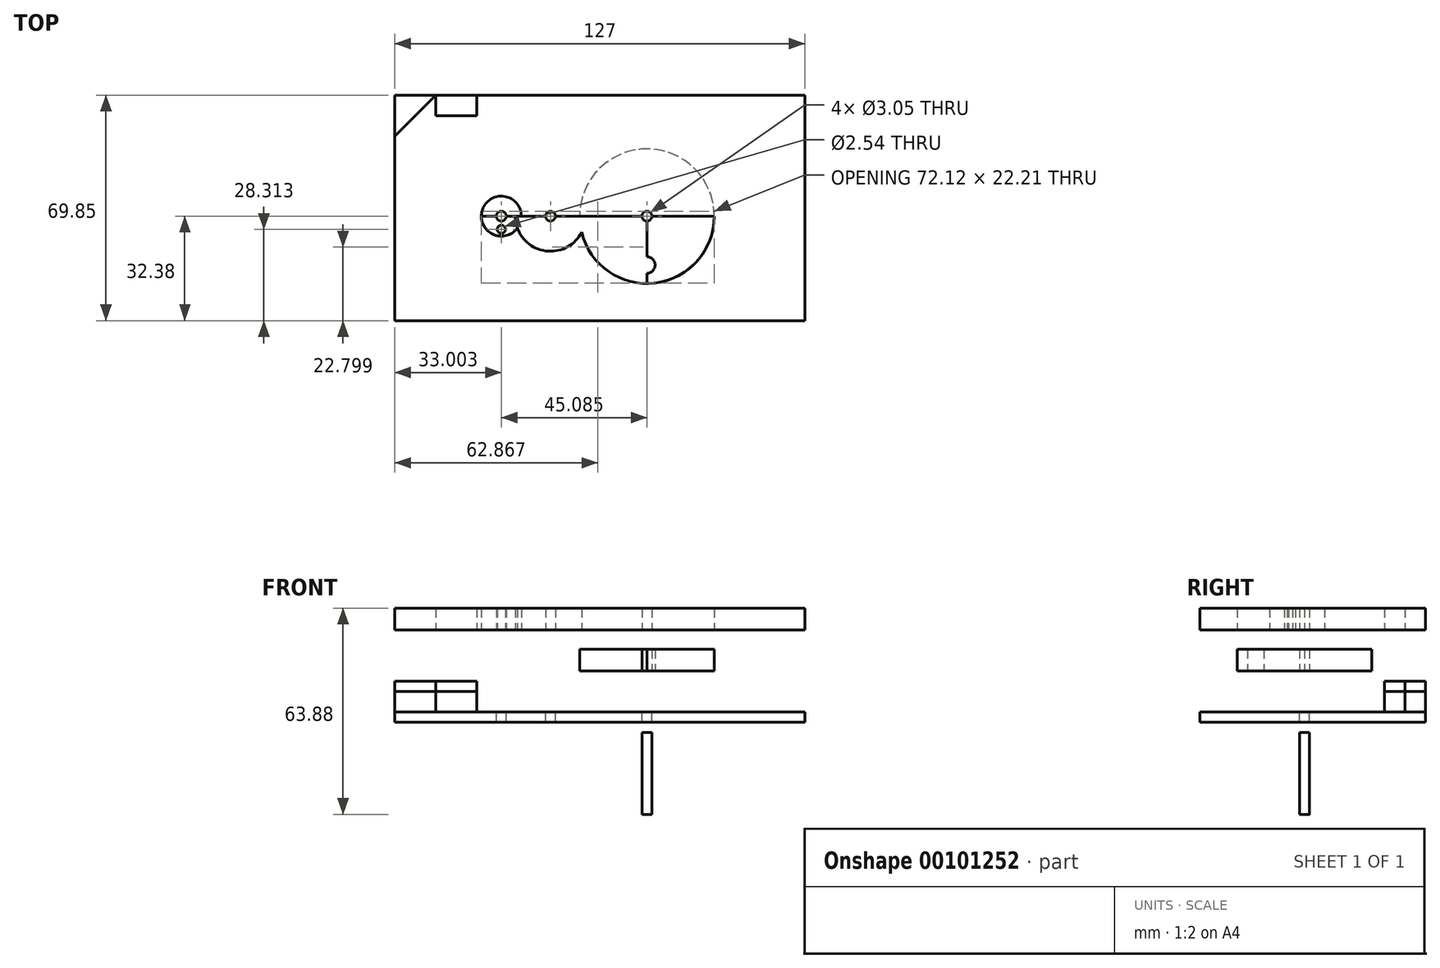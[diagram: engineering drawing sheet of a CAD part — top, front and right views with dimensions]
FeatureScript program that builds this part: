
annotation { "Feature Type Name" : "Feature", "Feature Type Description" : "" }
export const myFeature = defineFeature(function(context is Context, id is Id, definition is map)
    precondition{}
    {
        {
            var Q0;
            Q0=qCreatedBy(makeId("Top.planeOp"),FACE);
            var sketch = newSketch(context, id + "F0", { "sketchPlane" : qUnion([Q0])});
            skLineSegment(sketch, "E0", {"start": v(-33.34, 3.44) * mm, "end": v(-18.12, 3.44) * mm});
            skLineSegment(sketch, "E1", {"start": v(-18.12, 3.44) * mm, "end": v(11.75, 3.44) * mm});
            skCircle(sketch, "E2", {"center": v(-33.34, 3.44) * mm, "radius": 6.2 * mm});
            skCircle(sketch, "E3", {"center": v(11.75, 3.44) * mm, "radius": 20.84 * mm});
            skCircle(sketch, "E4", {"center": v(-18.12, 3.44) * mm, "radius": 10.86 * mm});
            skLineSegment(sketch, "E5.bottom", {"start": v(-66.34, 40.9) * mm, "end": v(60.66, 40.9) * mm});
            skLineSegment(sketch, "E5.top", {"start": v(-66.34, -28.94) * mm, "end": v(60.66, -28.94) * mm});
            skLineSegment(sketch, "E5.left", {"start": v(-66.34, 40.9) * mm, "end": v(-66.34, -28.94) * mm});
            skLineSegment(sketch, "E5.right", {"start": v(60.66, 40.9) * mm, "end": v(60.66, -28.94) * mm});
            skCircle(sketch, "E6", {"center": v(11.75, 3.44) * mm, "radius": 1.52 * mm});
            skCircle(sketch, "E7", {"center": v(-18.12, 3.44) * mm, "radius": 1.52 * mm});
            skCircle(sketch, "E8", {"center": v(-33.34, 3.44) * mm, "radius": 1.52 * mm});
            skLineSegment(sketch, "E9", {"start": v(11.75, 3.44) * mm, "end": v(11.75, -17.4) * mm});
            skLineSegment(sketch, "E10", {"start": v(-18.12, 3.44) * mm, "end": v(-18.27, -7.42) * mm});
            skLineSegment(sketch, "E11", {"start": v(-33.34, 3.44) * mm, "end": v(-33.34, -2.76) * mm});
            skCircle(sketch, "E12", {"center": v(11.75, -11.68) * mm, "radius": 2.54 * mm});
            skCircle(sketch, "E13", {"center": v(-18.23, -4.37) * mm, "radius": 1.9 * mm});
            skCircle(sketch, "E14", {"center": v(-33.34, -0.63) * mm, "radius": 1.27 * mm});
            skLineSegment(sketch, "E15", {"start": v(-53.64, 40.9) * mm, "end": v(-66.34, 28.2) * mm});
            skLineSegment(sketch, "E16", {"start": v(-53.64, 40.9) * mm, "end": v(-53.64, 34.56) * mm});
            skLineSegment(sketch, "E17", {"start": v(-53.64, 34.56) * mm, "end": v(-40.94, 34.56) * mm});
            skLineSegment(sketch, "E18", {"start": v(-40.94, 34.56) * mm, "end": v(-40.94, 40.9) * mm});
            skLineSegment(sketch, "E19", {"start": v(-39.54, 3.44) * mm, "end": v(32.59, 3.44) * mm});
            skLineSegment(sketch, "E20", {"start": v(-3.47, 3.44) * mm, "end": v(-3.47, 9.38) * mm});
            skSolve(sketch);
        }
        {
            var Q0;
            Q0=makeQuery(id+"F0.imprint","IMPRINT",FACE,{"disambiguationData":[TD([[makeQuery(id+"F0.imprint","IMPRINT",EDGE,{"derivedFrom":sQuery(id+"F0.wireOp",EDGE,"E5.bottom")}),-1.0]])]});
            var Q1;
            Q1=makeQuery(id+"F0.imprint","IMPRINT",FACE,{"disambiguationData":[TD([[makeQuery(id+"F0.imprint","IMPRINT",EDGE,{"derivedFrom":sQuery(id+"F0.wireOp",EDGE,"E6")}),-1.0]])]});
            var Q2;
            {var subQ6=sQuery(id+"F0.wireOp",EDGE,"E0");var subQ9=sQuery(id+"F0.wireOp",EDGE,"E2");var subQ10=makeQuery(id+"F0.imprint","INTERSECT",VERTEX,{"derivedFrom":[subQ6,subQ9]});Q2=makeQuery(id+"F0.imprint","IMPRINT",FACE,{"disambiguationData":[TD([[makeQuery(id+"F0.imprint","IMPRINT",EDGE,{"disambiguationData":[TD([[subQ10,-1.0]])],"derivedFrom":subQ6}),1.0]])]});}
            var Q3;
            Q3=makeQuery(id+"F0.imprint","IMPRINT",FACE,{"disambiguationData":[TD([[makeQuery(id+"F0.imprint","IMPRINT",EDGE,{"derivedFrom":sQuery(id+"F0.wireOp",EDGE,"E8")}),-1.0]])]});
            var Q4;
            {var subQ0=sQuery(id+"F0.wireOp",EDGE,"E4");var subQ1=sQuery(id+"F0.wireOp",EDGE,"E0");var subQ2=makeQuery(id+"F0.imprint","INTERSECT",VERTEX,{"derivedFrom":[subQ1,subQ0]});Q4=makeQuery(id+"F0.imprint","IMPRINT",FACE,{"disambiguationData":[TD([[makeQuery(id+"F0.imprint","IMPRINT",EDGE,{"disambiguationData":[TD([[subQ2,-1.0]])],"derivedFrom":subQ1}),-1.0]])]});}
            var Q5;
            {var subQ0=sQuery(id+"F0.wireOp",EDGE,"E4");var subQ1=sQuery(id+"F0.wireOp",EDGE,"E0");var subQ2=makeQuery(id+"F0.imprint","INTERSECT",VERTEX,{"derivedFrom":[subQ1,subQ0]});Q5=makeQuery(id+"F0.imprint","IMPRINT",FACE,{"disambiguationData":[TD([[makeQuery(id+"F0.imprint","IMPRINT",EDGE,{"disambiguationData":[TD([[subQ2,-1.0]])],"derivedFrom":subQ1}),1.0]])]});}
            var Q6;
            {var subQ0=sQuery(id+"F0.wireOp",EDGE,"E4");var subQ1=sQuery(id+"F0.wireOp",EDGE,"E1");var subQ2=makeQuery(id+"F0.imprint","INTERSECT",VERTEX,{"derivedFrom":[subQ1,subQ0]});Q6=makeQuery(id+"F0.imprint","IMPRINT",FACE,{"disambiguationData":[TD([[makeQuery(id+"F0.imprint","IMPRINT",EDGE,{"disambiguationData":[TD([[subQ2,1.0]])],"derivedFrom":subQ1}),-1.0]])]});}
            var Q7;
            {var subQ0=sQuery(id+"F0.wireOp",EDGE,"E4");var subQ1=sQuery(id+"F0.wireOp",EDGE,"E1");var subQ2=makeQuery(id+"F0.imprint","INTERSECT",VERTEX,{"derivedFrom":[subQ1,subQ0]});Q7=makeQuery(id+"F0.imprint","IMPRINT",FACE,{"disambiguationData":[TD([[makeQuery(id+"F0.imprint","IMPRINT",EDGE,{"disambiguationData":[TD([[subQ2,1.0]])],"derivedFrom":subQ1}),1.0]])]});}
            var Q8;
            {var subQ0=sQuery(id+"F0.wireOp",EDGE,"kLhhA65f-NG9x-GNjo-BDkE-ldiiMeL40Zhi");var subQ1=sQuery(id+"F0.wireOp",EDGE,"E11");var subQ2=makeQuery(id+"F0.imprint","INTERSECT",VERTEX,{"derivedFrom":[subQ1,subQ0]});Q8=makeQuery(id+"F0.imprint","IMPRINT",FACE,{"disambiguationData":[TD([[makeQuery(id+"F0.imprint","IMPRINT",EDGE,{"disambiguationData":[TD([[subQ2,-1.0]])],"derivedFrom":subQ1}),-1.0]])]});}
            var Q9;
            {var subQ0=sQuery(id+"F0.wireOp",EDGE,"8ZkhhjgY-9uin-yOEb-Jnnh-ZfXHKx15u7Ma");var subQ1=sQuery(id+"F0.wireOp",EDGE,"E11");var subQ2=makeQuery(id+"F0.imprint","INTERSECT",VERTEX,{"derivedFrom":[subQ1,subQ0]});Q9=makeQuery(id+"F0.imprint","IMPRINT",FACE,{"disambiguationData":[TD([[makeQuery(id+"F0.imprint","IMPRINT",EDGE,{"disambiguationData":[TD([[subQ2,-1.0]])],"derivedFrom":subQ1}),-1.0]])]});}
            var Q10;
            {var subQ0=sQuery(id+"F0.wireOp",EDGE,"kLhhA65f-NG9x-GNjo-BDkE-ldiiMeL40Zhi");var subQ1=sQuery(id+"F0.wireOp",EDGE,"E11");var subQ2=makeQuery(id+"F0.imprint","INTERSECT",VERTEX,{"derivedFrom":[subQ1,subQ0]});Q10=makeQuery(id+"F0.imprint","IMPRINT",FACE,{"disambiguationData":[TD([[makeQuery(id+"F0.imprint","IMPRINT",EDGE,{"disambiguationData":[TD([[subQ2,-1.0]])],"derivedFrom":subQ1}),1.0]])]});}
            var Q11;
            {var subQ5=sQuery(id+"F0.wireOp",EDGE,"8ZkhhjgY-9uin-yOEb-Jnnh-ZfXHKx15u7Ma");var subQ7=sQuery(id+"F0.wireOp",EDGE,"E11");var subQ9=makeQuery(id+"F0.imprint","INTERSECT",VERTEX,{"derivedFrom":[subQ7,subQ5]});Q11=makeQuery(id+"F0.imprint","IMPRINT",FACE,{"disambiguationData":[TD([[makeQuery(id+"F0.imprint","IMPRINT",EDGE,{"disambiguationData":[TD([[subQ9,-1.0]])],"derivedFrom":subQ7}),1.0]])]});}
            var Q12;
            {var subQ0=sQuery(id+"F0.wireOp",EDGE,"8ZkhhjgY-9uin-yOEb-Jnnh-ZfXHKx15u7Ma");var subQ1=sQuery(id+"F0.wireOp",EDGE,"klJGlrE8-QjUh-doVU-lAX6-h4YymrU0E4Rz");var subQ2=makeQuery(id+"F0.imprint","INTERSECT",VERTEX,{"derivedFrom":[subQ1,subQ0]});Q12=makeQuery(id+"F0.imprint","IMPRINT",FACE,{"disambiguationData":[TD([[makeQuery(id+"F0.imprint","IMPRINT",EDGE,{"disambiguationData":[TD([[subQ2,-1.0]])],"derivedFrom":subQ1}),1.0]])]});}
            var Q13;
            {var subQ0=sQuery(id+"F0.wireOp",EDGE,"Twp39fOy-9zCw-zEIi-sOgK-c6f8t6DE6qxe");var subQ1=sQuery(id+"F0.wireOp",EDGE,"klJGlrE8-QjUh-doVU-lAX6-h4YymrU0E4Rz");var subQ2=makeQuery(id+"F0.imprint","INTERSECT",VERTEX,{"derivedFrom":[subQ1,subQ0]});Q13=makeQuery(id+"F0.imprint","IMPRINT",FACE,{"disambiguationData":[TD([[makeQuery(id+"F0.imprint","IMPRINT",EDGE,{"disambiguationData":[TD([[subQ2,1.0]])],"derivedFrom":subQ1}),-1.0]])]});}
            var Q14;
            {var subQ15=sQuery(id+"F0.wireOp",EDGE,"E8");var subQ20=sQuery(id+"F0.wireOp",EDGE,"E0");var subQ21=makeQuery(id+"F0.imprint","INTERSECT",VERTEX,{"derivedFrom":[subQ20,subQ15]});Q14=makeQuery(id+"F0.imprint","IMPRINT",FACE,{"disambiguationData":[TD([[makeQuery(id+"F0.imprint","IMPRINT",EDGE,{"disambiguationData":[TD([[subQ21,-1.0]])],"derivedFrom":subQ20}),-1.0]])]});}
            var Q15;
            {var subQ1=sQuery(id+"F0.wireOp",EDGE,"E7");var subQ15=sQuery(id+"F0.wireOp",EDGE,"E1");var subQ20=makeQuery(id+"F0.imprint","INTERSECT",VERTEX,{"derivedFrom":[subQ15,subQ1]});Q15=makeQuery(id+"F0.imprint","IMPRINT",FACE,{"disambiguationData":[TD([[makeQuery(id+"F0.imprint","IMPRINT",EDGE,{"disambiguationData":[TD([[subQ20,-1.0]])],"derivedFrom":subQ15}),-1.0]])]});}
            var Q16;
            {var subQ0=sQuery(id+"F0.wireOp",EDGE,"5052977a-4594-4a14-8260-0f098557343a");var subQ1=sQuery(id+"F0.wireOp",EDGE,"0b054047-080a-4dd0-b0d3-495809a409b5");var subQ2=makeQuery(id+"F0.imprint","INTERSECT",VERTEX,{"derivedFrom":[subQ1,subQ0]});Q16=makeQuery(id+"F0.imprint","IMPRINT",FACE,{"disambiguationData":[TD([[makeQuery(id+"F0.imprint","IMPRINT",EDGE,{"disambiguationData":[TD([[subQ2,-1.0]])],"derivedFrom":subQ1}),1.0]])]});}
            var Q17;
            {var subQ0=sQuery(id+"F0.wireOp",EDGE,"5fe9bd24-ed45-42ec-b14b-03178a733d0b");var subQ1=sQuery(id+"F0.wireOp",EDGE,"5052977a-4594-4a14-8260-0f098557343a");var subQ2=makeQuery(id+"F0.imprint","INTERSECT",VERTEX,{"derivedFrom":[subQ1,subQ0]});Q17=makeQuery(id+"F0.imprint","IMPRINT",FACE,{"disambiguationData":[TD([[makeQuery(id+"F0.imprint","IMPRINT",EDGE,{"disambiguationData":[TD([[subQ2,1.0]])],"derivedFrom":subQ1}),-1.0]])]});}
            var Q18;
            {var subQ0=sQuery(id+"F0.wireOp",EDGE,"AysafuJL-hgFW-WlnW-CkoB-AsvmlXaG8yLZ");var subQ1=sQuery(id+"F0.wireOp",EDGE,"0b054047-080a-4dd0-b0d3-495809a409b5");var subQ2=makeQuery(id+"F0.imprint","INTERSECT",VERTEX,{"derivedFrom":[subQ1,subQ0]});Q18=makeQuery(id+"F0.imprint","IMPRINT",FACE,{"disambiguationData":[TD([[makeQuery(id+"F0.imprint","IMPRINT",EDGE,{"disambiguationData":[TD([[subQ2,-1.0]])],"derivedFrom":subQ1}),-1.0]])]});}
            var Q19;
            {var subQ0=sQuery(id+"F0.wireOp",EDGE,"AysafuJL-hgFW-WlnW-CkoB-AsvmlXaG8yLZ");var subQ1=sQuery(id+"F0.wireOp",EDGE,"0b054047-080a-4dd0-b0d3-495809a409b5");var subQ2=makeQuery(id+"F0.imprint","INTERSECT",VERTEX,{"derivedFrom":[subQ1,subQ0]});Q19=makeQuery(id+"F0.imprint","IMPRINT",FACE,{"disambiguationData":[TD([[makeQuery(id+"F0.imprint","IMPRINT",EDGE,{"disambiguationData":[TD([[subQ2,-1.0]])],"derivedFrom":subQ1}),1.0]])]});}
            var Q20;
            {var subQ0=sQuery(id+"F0.wireOp",EDGE,"AysafuJL-hgFW-WlnW-CkoB-AsvmlXaG8yLZ");var subQ1=sQuery(id+"F0.wireOp",EDGE,"5fe9bd24-ed45-42ec-b14b-03178a733d0b");var subQ2=makeQuery(id+"F0.imprint","INTERSECT",VERTEX,{"derivedFrom":[subQ1,subQ0]});Q20=makeQuery(id+"F0.imprint","IMPRINT",FACE,{"disambiguationData":[TD([[makeQuery(id+"F0.imprint","IMPRINT",EDGE,{"disambiguationData":[TD([[subQ2,-1.0]])],"derivedFrom":subQ1}),-1.0]])]});}
            var Q21;
            {var subQ0=sQuery(id+"F0.wireOp",EDGE,"AysafuJL-hgFW-WlnW-CkoB-AsvmlXaG8yLZ");var subQ1=sQuery(id+"F0.wireOp",EDGE,"5fe9bd24-ed45-42ec-b14b-03178a733d0b");var subQ2=makeQuery(id+"F0.imprint","INTERSECT",VERTEX,{"derivedFrom":[subQ1,subQ0]});Q21=makeQuery(id+"F0.imprint","IMPRINT",FACE,{"disambiguationData":[TD([[makeQuery(id+"F0.imprint","IMPRINT",EDGE,{"disambiguationData":[TD([[subQ2,-1.0]])],"derivedFrom":subQ1}),1.0]])]});}
            var Q22;
            {var subQ0=sQuery(id+"F0.wireOp",EDGE,"fyqTDLPH-M1B6-Q20Z-5p9l-KNEeE5BD3CPC");var subQ1=sQuery(id+"F0.wireOp",EDGE,"5fe9bd24-ed45-42ec-b14b-03178a733d0b");var subQ2=makeQuery(id+"F0.imprint","INTERSECT",VERTEX,{"derivedFrom":[subQ1,subQ0]});Q22=makeQuery(id+"F0.imprint","IMPRINT",FACE,{"disambiguationData":[TD([[makeQuery(id+"F0.imprint","IMPRINT",EDGE,{"disambiguationData":[TD([[subQ2,1.0]])],"derivedFrom":subQ1}),-1.0]])]});}
            var Q23;
            {var subQ0=sQuery(id+"F0.wireOp",EDGE,"fyqTDLPH-M1B6-Q20Z-5p9l-KNEeE5BD3CPC");var subQ1=sQuery(id+"F0.wireOp",EDGE,"0b054047-080a-4dd0-b0d3-495809a409b5");var subQ2=makeQuery(id+"F0.imprint","INTERSECT",VERTEX,{"derivedFrom":[subQ1,subQ0]});Q23=makeQuery(id+"F0.imprint","IMPRINT",FACE,{"disambiguationData":[TD([[makeQuery(id+"F0.imprint","IMPRINT",EDGE,{"disambiguationData":[TD([[subQ2,1.0]])],"derivedFrom":subQ1}),1.0]])]});}
            var Q24;
            {var subQ7=sQuery(id+"F0.wireOp",EDGE,"E2");var subQ8=sQuery(id+"F0.wireOp",EDGE,"E0");var subQ9=makeQuery(id+"F0.imprint","INTERSECT",VERTEX,{"derivedFrom":[subQ8,subQ7]});Q24=makeQuery(id+"F0.imprint","IMPRINT",FACE,{"disambiguationData":[TD([[makeQuery(id+"F0.imprint","IMPRINT",EDGE,{"disambiguationData":[TD([[subQ9,-1.0]])],"derivedFrom":subQ8}),-1.0]])]});}
            var Q25;
            {var subQ3=sQuery(id+"F0.wireOp",EDGE,"8Nk1CSgT-vGRZ-uZ8g-dRgu-DJPxAlyrmn83");var subQ5=sQuery(id+"F0.wireOp",EDGE,"kqWuPtpw-YDnI-BRKi-M2Yr-v8eZbLSoqUS7");var subQ6=makeQuery(id+"F0.imprint","INTERSECT",VERTEX,{"derivedFrom":[subQ5,subQ3]});Q25=makeQuery(id+"F0.imprint","IMPRINT",FACE,{"disambiguationData":[TD([[makeQuery(id+"F0.imprint","IMPRINT",EDGE,{"disambiguationData":[TD([[subQ6,-1.0]])],"derivedFrom":subQ5}),-1.0]])]});}
            var Q26;
            {var subQ0=sQuery(id+"F0.wireOp",EDGE,"8Nk1CSgT-vGRZ-uZ8g-dRgu-DJPxAlyrmn83");var subQ1=sQuery(id+"F0.wireOp",EDGE,"kqWuPtpw-YDnI-BRKi-M2Yr-v8eZbLSoqUS7");var subQ2=makeQuery(id+"F0.imprint","INTERSECT",VERTEX,{"derivedFrom":[subQ1,subQ0]});Q26=makeQuery(id+"F0.imprint","IMPRINT",FACE,{"disambiguationData":[TD([[makeQuery(id+"F0.imprint","IMPRINT",EDGE,{"disambiguationData":[TD([[subQ2,-1.0]])],"derivedFrom":subQ1}),1.0]])]});}
            var Q27;
            {var subQ3=sQuery(id+"F0.wireOp",EDGE,"8Nk1CSgT-vGRZ-uZ8g-dRgu-DJPxAlyrmn83");var subQ5=sQuery(id+"F0.wireOp",EDGE,"PzxtjhWC-1IdU-xVl6-3CaP-CxFpPKaMt4wZ");var subQ7=makeQuery(id+"F0.imprint","INTERSECT",VERTEX,{"derivedFrom":[subQ5,subQ3]});Q27=makeQuery(id+"F0.imprint","IMPRINT",FACE,{"disambiguationData":[TD([[makeQuery(id+"F0.imprint","IMPRINT",EDGE,{"disambiguationData":[TD([[subQ7,-1.0]])],"derivedFrom":subQ5}),1.0]])]});}
            var Q28;
            {var subQ0=sQuery(id+"F0.wireOp",EDGE,"8Nk1CSgT-vGRZ-uZ8g-dRgu-DJPxAlyrmn83");var subQ1=sQuery(id+"F0.wireOp",EDGE,"PzxtjhWC-1IdU-xVl6-3CaP-CxFpPKaMt4wZ");var subQ2=makeQuery(id+"F0.imprint","INTERSECT",VERTEX,{"derivedFrom":[subQ1,subQ0]});Q28=makeQuery(id+"F0.imprint","IMPRINT",FACE,{"disambiguationData":[TD([[makeQuery(id+"F0.imprint","IMPRINT",EDGE,{"disambiguationData":[TD([[subQ2,-1.0]])],"derivedFrom":subQ1}),-1.0]])]});}
            var Q29;
            {var subQ0=sQuery(id+"F0.wireOp",EDGE,"qKIvb24z-OBM9-jN8k-dcP5-Cy2G3Ynz1Tdz");var subQ1=sQuery(id+"F0.wireOp",EDGE,"E9");var subQ2=makeQuery(id+"F0.imprint","INTERSECT",VERTEX,{"derivedFrom":[subQ1,subQ0]});Q29=makeQuery(id+"F0.imprint","IMPRINT",FACE,{"disambiguationData":[TD([[makeQuery(id+"F0.imprint","IMPRINT",EDGE,{"disambiguationData":[TD([[subQ2,-1.0]])],"derivedFrom":subQ1}),1.0]])]});}
            var Q30;
            {var subQ0=sQuery(id+"F0.wireOp",EDGE,"qKIvb24z-OBM9-jN8k-dcP5-Cy2G3Ynz1Tdz");var subQ1=sQuery(id+"F0.wireOp",EDGE,"E9");var subQ2=makeQuery(id+"F0.imprint","INTERSECT",VERTEX,{"derivedFrom":[subQ1,subQ0]});Q30=makeQuery(id+"F0.imprint","IMPRINT",FACE,{"disambiguationData":[TD([[makeQuery(id+"F0.imprint","IMPRINT",EDGE,{"disambiguationData":[TD([[subQ2,-1.0]])],"derivedFrom":subQ1}),-1.0]])]});}
            var Q31;
            {var subQ0=sQuery(id+"F0.wireOp",EDGE,"kqWuPtpw-YDnI-BRKi-M2Yr-v8eZbLSoqUS7");var subQ1=sQuery(id+"F0.wireOp",EDGE,"5nWJJ5fH-ccEX-65kx-TIwQ-cNrI7n7U708l");var subQ2=makeQuery(id+"F0.imprint","INTERSECT",VERTEX,{"derivedFrom":[subQ1,subQ0]});Q31=makeQuery(id+"F0.imprint","IMPRINT",FACE,{"disambiguationData":[TD([[makeQuery(id+"F0.imprint","IMPRINT",EDGE,{"disambiguationData":[TD([[subQ2,1.0]])],"derivedFrom":subQ0}),-1.0]])]});}
            var Q32;
            {var subQ0=sQuery(id+"F0.wireOp",EDGE,"5nWJJ5fH-ccEX-65kx-TIwQ-cNrI7n7U708l");var subQ1=sQuery(id+"F0.wireOp",EDGE,"PzxtjhWC-1IdU-xVl6-3CaP-CxFpPKaMt4wZ");var subQ2=makeQuery(id+"F0.imprint","INTERSECT",VERTEX,{"derivedFrom":[subQ1,subQ0]});Q32=makeQuery(id+"F0.imprint","IMPRINT",FACE,{"disambiguationData":[TD([[makeQuery(id+"F0.imprint","IMPRINT",EDGE,{"disambiguationData":[TD([[subQ2,1.0]])],"derivedFrom":subQ1}),1.0]])]});}
            var Q33;
            {var subQ0=sQuery(id+"F0.wireOp",EDGE,"E12");var subQ1=sQuery(id+"F0.wireOp",EDGE,"E9");var subQ2=makeQuery(id+"F0.imprint","INTERSECT",VERTEX,{"disambiguationData":[OD(0.0)],"derivedFrom":[subQ1,subQ0]});Q33=makeQuery(id+"F0.imprint","IMPRINT",FACE,{"disambiguationData":[TD([[makeQuery(id+"F0.imprint","IMPRINT",EDGE,{"disambiguationData":[TD([[subQ2,-1.0]])],"derivedFrom":subQ1}),1.0]])]});}
            var Q34;
            {var subQ0=sQuery(id+"F0.wireOp",EDGE,"E13");var subQ1=sQuery(id+"F0.wireOp",EDGE,"E10");var subQ2=makeQuery(id+"F0.imprint","INTERSECT",VERTEX,{"disambiguationData":[OD(0.0)],"derivedFrom":[subQ1,subQ0]});Q34=makeQuery(id+"F0.imprint","IMPRINT",FACE,{"disambiguationData":[TD([[makeQuery(id+"F0.imprint","IMPRINT",EDGE,{"disambiguationData":[TD([[subQ2,-1.0]])],"derivedFrom":subQ1}),1.0]])]});}
            var Q35;
            {var subQ0=sQuery(id+"F0.wireOp",EDGE,"E14");var subQ1=sQuery(id+"F0.wireOp",EDGE,"E11");var subQ2=makeQuery(id+"F0.imprint","INTERSECT",VERTEX,{"disambiguationData":[OD(0.0)],"derivedFrom":[subQ1,subQ0]});Q35=makeQuery(id+"F0.imprint","IMPRINT",FACE,{"disambiguationData":[TD([[makeQuery(id+"F0.imprint","IMPRINT",EDGE,{"disambiguationData":[TD([[subQ2,-1.0]])],"derivedFrom":subQ1}),-1.0]])]});}
            var Q36;
            {var subQ0=sQuery(id+"F0.wireOp",EDGE,"E14");var subQ1=sQuery(id+"F0.wireOp",EDGE,"E11");var subQ2=makeQuery(id+"F0.imprint","INTERSECT",VERTEX,{"disambiguationData":[OD(0.0)],"derivedFrom":[subQ1,subQ0]});Q36=makeQuery(id+"F0.imprint","IMPRINT",FACE,{"disambiguationData":[TD([[makeQuery(id+"F0.imprint","IMPRINT",EDGE,{"disambiguationData":[TD([[subQ2,-1.0]])],"derivedFrom":subQ1}),1.0]])]});}
            var Q37;
            {var subQ0=sQuery(id+"F0.wireOp",EDGE,"E13");var subQ1=sQuery(id+"F0.wireOp",EDGE,"E10");var subQ2=makeQuery(id+"F0.imprint","INTERSECT",VERTEX,{"disambiguationData":[OD(0.0)],"derivedFrom":[subQ1,subQ0]});Q37=makeQuery(id+"F0.imprint","IMPRINT",FACE,{"disambiguationData":[TD([[makeQuery(id+"F0.imprint","IMPRINT",EDGE,{"disambiguationData":[TD([[subQ2,-1.0]])],"derivedFrom":subQ1}),-1.0]])]});}
            var Q38;
            {var subQ0=sQuery(id+"F0.wireOp",EDGE,"E12");var subQ1=sQuery(id+"F0.wireOp",EDGE,"E9");var subQ2=makeQuery(id+"F0.imprint","INTERSECT",VERTEX,{"disambiguationData":[OD(0.0)],"derivedFrom":[subQ1,subQ0]});Q38=makeQuery(id+"F0.imprint","IMPRINT",FACE,{"disambiguationData":[TD([[makeQuery(id+"F0.imprint","IMPRINT",EDGE,{"disambiguationData":[TD([[subQ2,-1.0]])],"derivedFrom":subQ1}),-1.0]])]});}
            var Q39;
            {var subQ0=sQuery(id+"F0.wireOp",EDGE,"E16");Q39=makeQuery(id+"F0.imprint","IMPRINT",FACE,{"disambiguationData":[TD([[makeQuery(id+"F0.imprint","IMPRINT",EDGE,{"derivedFrom":subQ0}),1.0]])]});}
            var Q40;
            {var subQ1=sQuery(id+"F0.wireOp",EDGE,"E5.top");Q40=makeQuery(id+"F0.imprint","IMPRINT",FACE,{"disambiguationData":[TD([[makeQuery(id+"F0.imprint","IMPRINT",EDGE,{"derivedFrom":subQ1}),1.0]])]});}
            var Q41;
            {var subQ6=sQuery(id+"F0.wireOp",EDGE,"E19");var subQ10=sQuery(id+"F0.wireOp",EDGE,"E3");var subQ12=makeQuery(id+"F0.imprint","INTERSECT",VERTEX,{"disambiguationData":[OD(1.0)],"derivedFrom":[subQ10,subQ6]});Q41=makeQuery(id+"F0.imprint","IMPRINT",FACE,{"disambiguationData":[TD([[makeQuery(id+"F0.imprint","IMPRINT",EDGE,{"disambiguationData":[TD([[subQ12,-1.0]])],"derivedFrom":subQ10}),-1.0]])]});}
            var Q42;
            {var subQ5=sQuery(id+"F0.wireOp",EDGE,"E19");var subQ9=sQuery(id+"F0.wireOp",EDGE,"E2");var subQ11=makeQuery(id+"F0.imprint","INTERSECT",VERTEX,{"disambiguationData":[OD(1.0)],"derivedFrom":[subQ9,subQ5]});Q42=makeQuery(id+"F0.imprint","IMPRINT",FACE,{"disambiguationData":[TD([[makeQuery(id+"F0.imprint","IMPRINT",EDGE,{"disambiguationData":[TD([[subQ11,1.0]])],"derivedFrom":subQ9}),-1.0]])]});}
            var Q43;
            {var subQ4=sQuery(id+"F0.wireOp",EDGE,"E4");var subQ5=sQuery(id+"F0.wireOp",EDGE,"E2");var subQ6=makeQuery(id+"F0.imprint","INTERSECT",VERTEX,{"disambiguationData":[OD(0.0)],"derivedFrom":[subQ5,subQ4]});Q43=makeQuery(id+"F0.imprint","IMPRINT",FACE,{"disambiguationData":[TD([[makeQuery(id+"F0.imprint","IMPRINT",EDGE,{"disambiguationData":[TD([[subQ6,1.0]])],"derivedFrom":subQ5}),-1.0]])]});}
            var Q44;
            {var subQ0=sQuery(id+"F0.wireOp",EDGE,"E4");var subQ1=sQuery(id+"F0.wireOp",EDGE,"E3");var subQ2=makeQuery(id+"F0.imprint","INTERSECT",VERTEX,{"disambiguationData":[OD(0.0)],"derivedFrom":[subQ1,subQ0]});Q44=makeQuery(id+"F0.imprint","IMPRINT",FACE,{"disambiguationData":[TD([[makeQuery(id+"F0.imprint","IMPRINT",EDGE,{"disambiguationData":[TD([[subQ2,-1.0]])],"derivedFrom":subQ1}),1.0]])]});}
            var Q45;
            {var subQ0=sQuery(id+"F0.wireOp",EDGE,"E19");var subQ1=sQuery(id+"F0.wireOp",EDGE,"E3");var subQ2=makeQuery(id+"F0.imprint","INTERSECT",VERTEX,{"disambiguationData":[OD(1.0)],"derivedFrom":[subQ1,subQ0]});Q45=makeQuery(id+"F0.imprint","IMPRINT",FACE,{"disambiguationData":[TD([[makeQuery(id+"F0.imprint","IMPRINT",EDGE,{"disambiguationData":[TD([[subQ2,-1.0]])],"derivedFrom":subQ1}),1.0]])]});}
            var Q46;
            {var subQ0=sQuery(id+"F0.wireOp",EDGE,"E4");var subQ1=sQuery(id+"F0.wireOp",EDGE,"E2");var subQ2=makeQuery(id+"F0.imprint","INTERSECT",VERTEX,{"disambiguationData":[OD(0.0)],"derivedFrom":[subQ1,subQ0]});Q46=makeQuery(id+"F0.imprint","IMPRINT",FACE,{"disambiguationData":[TD([[makeQuery(id+"F0.imprint","IMPRINT",EDGE,{"disambiguationData":[TD([[subQ2,1.0]])],"derivedFrom":subQ1}),1.0]])]});}
            var Q47;
            {var subQ0=sQuery(id+"F0.wireOp",EDGE,"E19");var subQ1=sQuery(id+"F0.wireOp",EDGE,"E2");var subQ2=makeQuery(id+"F0.imprint","INTERSECT",VERTEX,{"disambiguationData":[OD(1.0)],"derivedFrom":[subQ1,subQ0]});Q47=makeQuery(id+"F0.imprint","IMPRINT",FACE,{"disambiguationData":[TD([[makeQuery(id+"F0.imprint","IMPRINT",EDGE,{"disambiguationData":[TD([[subQ2,1.0]])],"derivedFrom":subQ1}),1.0]])]});}
            extrude(context, id + "F1", {"entities" : qUnion([Q0, Q1, Q2, Q3, Q4, Q5, Q6, Q7, Q8, Q9, Q10, Q11, Q12, Q13, Q14, Q15, Q16, Q17, Q18, Q19, Q20, Q21, Q22, Q23, Q24, Q25, Q26, Q27, Q28, Q29, Q30, Q31, Q32, Q33, Q34, Q35, Q36, Q37, Q38, Q39, Q40, Q41, Q42, Q43, Q44, Q45, Q46, Q47]), "oppositeDirection" : true, "depth" : 3.17 * mm});
        }
        {
            var Q0;
            {var subQ0=sQuery(id+"F0.wireOp",EDGE,"E19");var subQ4=sQuery(id+"F0.wireOp",EDGE,"E2");var subQ5=makeQuery(id+"F0.imprint","INTERSECT",VERTEX,{"disambiguationData":[OD(0.0)],"derivedFrom":[subQ4,subQ0]});Q0=makeQuery(id+"F0.imprint","IMPRINT",FACE,{"disambiguationData":[TD([[makeQuery(id+"F0.imprint","IMPRINT",EDGE,{"disambiguationData":[TD([[subQ5,1.0]])],"derivedFrom":subQ4}),1.0]])]});}
            var Q1;
            {var subQ0=sQuery(id+"F0.wireOp",EDGE,"E11");var subQ1=sQuery(id+"F0.wireOp",EDGE,"E2");var subQ2=makeQuery(id+"F0.imprint","INTERSECT",VERTEX,{"derivedFrom":[subQ1,subQ0]});Q1=makeQuery(id+"F0.imprint","IMPRINT",FACE,{"disambiguationData":[TD([[makeQuery(id+"F0.imprint","IMPRINT",EDGE,{"disambiguationData":[TD([[subQ2,1.0]])],"derivedFrom":subQ1}),1.0]])]});}
            var Q2;
            {var subQ0=sQuery(id+"F0.wireOp",EDGE,"E11");var subQ6=sQuery(id+"F0.wireOp",EDGE,"E2");var subQ10=makeQuery(id+"F0.imprint","INTERSECT",VERTEX,{"derivedFrom":[subQ6,subQ0]});Q2=makeQuery(id+"F0.imprint","IMPRINT",FACE,{"disambiguationData":[TD([[makeQuery(id+"F0.imprint","IMPRINT",EDGE,{"disambiguationData":[TD([[subQ10,-1.0]])],"derivedFrom":subQ6}),1.0]])]});}
            var Q3;
            {var subQ0=sQuery(id+"F0.wireOp",EDGE,"E19");var subQ1=sQuery(id+"F0.wireOp",EDGE,"E2");var subQ2=makeQuery(id+"F0.imprint","INTERSECT",VERTEX,{"disambiguationData":[OD(1.0)],"derivedFrom":[subQ1,subQ0]});Q3=makeQuery(id+"F0.imprint","IMPRINT",FACE,{"disambiguationData":[TD([[makeQuery(id+"F0.imprint","IMPRINT",EDGE,{"disambiguationData":[TD([[subQ2,1.0]])],"derivedFrom":subQ1}),1.0]])]});}
            var Q4;
            {var subQ0=sQuery(id+"F0.wireOp",EDGE,"E4");var subQ1=sQuery(id+"F0.wireOp",EDGE,"E2");var subQ2=makeQuery(id+"F0.imprint","INTERSECT",VERTEX,{"disambiguationData":[OD(0.0)],"derivedFrom":[subQ1,subQ0]});Q4=makeQuery(id+"F0.imprint","IMPRINT",FACE,{"disambiguationData":[TD([[makeQuery(id+"F0.imprint","IMPRINT",EDGE,{"disambiguationData":[TD([[subQ2,1.0]])],"derivedFrom":subQ1}),1.0]])]});}
            extrude(context, id + "F2", {"entities" : qUnion([Q0, Q1, Q2, Q3, Q4]), "depth" : 32.13 * mm, "hasSecondDirection" : true, "secondDirectionOppositeDirection" : false, "secondDirectionDepth" : 25.4 * mm});
        }
        {
            var Q0;
            {var subQ4=sQuery(id+"F0.wireOp",EDGE,"E4");var subQ5=sQuery(id+"F0.wireOp",EDGE,"E2");var subQ6=makeQuery(id+"F0.imprint","INTERSECT",VERTEX,{"disambiguationData":[OD(0.0)],"derivedFrom":[subQ5,subQ4]});Q0=makeQuery(id+"F0.imprint","IMPRINT",FACE,{"disambiguationData":[TD([[makeQuery(id+"F0.imprint","IMPRINT",EDGE,{"disambiguationData":[TD([[subQ6,1.0]])],"derivedFrom":subQ5}),-1.0]])]});}
            var Q1;
            {var subQ5=sQuery(id+"F0.wireOp",EDGE,"E19");var subQ9=sQuery(id+"F0.wireOp",EDGE,"E2");var subQ11=makeQuery(id+"F0.imprint","INTERSECT",VERTEX,{"disambiguationData":[OD(1.0)],"derivedFrom":[subQ9,subQ5]});Q1=makeQuery(id+"F0.imprint","IMPRINT",FACE,{"disambiguationData":[TD([[makeQuery(id+"F0.imprint","IMPRINT",EDGE,{"disambiguationData":[TD([[subQ11,1.0]])],"derivedFrom":subQ9}),-1.0]])]});}
            var Q2;
            {var subQ6=sQuery(id+"F0.wireOp",EDGE,"E19");var subQ10=sQuery(id+"F0.wireOp",EDGE,"E3");var subQ12=makeQuery(id+"F0.imprint","INTERSECT",VERTEX,{"disambiguationData":[OD(1.0)],"derivedFrom":[subQ10,subQ6]});Q2=makeQuery(id+"F0.imprint","IMPRINT",FACE,{"disambiguationData":[TD([[makeQuery(id+"F0.imprint","IMPRINT",EDGE,{"disambiguationData":[TD([[subQ12,-1.0]])],"derivedFrom":subQ10}),-1.0]])]});}
            var Q3;
            {var subQ0=sQuery(id+"F0.wireOp",EDGE,"E4");var subQ1=sQuery(id+"F0.wireOp",EDGE,"E2");var subQ2=makeQuery(id+"F0.imprint","INTERSECT",VERTEX,{"disambiguationData":[OD(0.0)],"derivedFrom":[subQ1,subQ0]});Q3=makeQuery(id+"F0.imprint","IMPRINT",FACE,{"disambiguationData":[TD([[makeQuery(id+"F0.imprint","IMPRINT",EDGE,{"disambiguationData":[TD([[subQ2,1.0]])],"derivedFrom":subQ1}),1.0]])]});}
            var Q4;
            {var subQ0=sQuery(id+"F0.wireOp",EDGE,"E19");var subQ1=sQuery(id+"F0.wireOp",EDGE,"E2");var subQ2=makeQuery(id+"F0.imprint","INTERSECT",VERTEX,{"disambiguationData":[OD(1.0)],"derivedFrom":[subQ1,subQ0]});Q4=makeQuery(id+"F0.imprint","IMPRINT",FACE,{"disambiguationData":[TD([[makeQuery(id+"F0.imprint","IMPRINT",EDGE,{"disambiguationData":[TD([[subQ2,1.0]])],"derivedFrom":subQ1}),1.0]])]});}
            var Q5;
            {var subQ0=sQuery(id+"F0.wireOp",EDGE,"E4");var subQ1=sQuery(id+"F0.wireOp",EDGE,"E3");var subQ2=makeQuery(id+"F0.imprint","INTERSECT",VERTEX,{"disambiguationData":[OD(0.0)],"derivedFrom":[subQ1,subQ0]});Q5=makeQuery(id+"F0.imprint","IMPRINT",FACE,{"disambiguationData":[TD([[makeQuery(id+"F0.imprint","IMPRINT",EDGE,{"disambiguationData":[TD([[subQ2,-1.0]])],"derivedFrom":subQ1}),1.0]])]});}
            var Q6;
            {var subQ0=sQuery(id+"F0.wireOp",EDGE,"E19");var subQ1=sQuery(id+"F0.wireOp",EDGE,"E3");var subQ2=makeQuery(id+"F0.imprint","INTERSECT",VERTEX,{"disambiguationData":[OD(1.0)],"derivedFrom":[subQ1,subQ0]});Q6=makeQuery(id+"F0.imprint","IMPRINT",FACE,{"disambiguationData":[TD([[makeQuery(id+"F0.imprint","IMPRINT",EDGE,{"disambiguationData":[TD([[subQ2,-1.0]])],"derivedFrom":subQ1}),1.0]])]});}
            extrude(context, id + "F3", {"entities" : qUnion([Q0, Q1, Q2, Q3, Q4, Q5, Q6]), "depth" : 32.13 * mm, "hasSecondDirection" : true, "secondDirectionOppositeDirection" : false, "secondDirectionDepth" : 25.4 * mm});
        }
        {
            var Q0;
            {var subQ0=sQuery(id+"F0.wireOp",EDGE,"E19");var subQ9=makeQuery(id+"F0.imprint","IMPRINT",VERTEX,{"derivedFrom":subQ0});Q0=makeQuery(id+"F0.imprint","IMPRINT",FACE,{"disambiguationData":[TD([[makeQuery(id+"F0.imprint","IMPRINT",EDGE,{"disambiguationData":[TD([[subQ9,1.0]])],"derivedFrom":subQ0}),1.0]])]});}
            var Q1;
            {var subQ0=sQuery(id+"F0.wireOp",EDGE,"E4");var subQ1=sQuery(id+"F0.wireOp",EDGE,"E3");var subQ2=makeQuery(id+"F0.imprint","INTERSECT",VERTEX,{"disambiguationData":[OD(0.0)],"derivedFrom":[subQ1,subQ0]});Q1=makeQuery(id+"F0.imprint","IMPRINT",FACE,{"disambiguationData":[TD([[makeQuery(id+"F0.imprint","IMPRINT",EDGE,{"disambiguationData":[TD([[subQ2,-1.0]])],"derivedFrom":subQ1}),1.0]])]});}
            var Q2;
            {var subQ0=sQuery(id+"F0.wireOp",EDGE,"E19");var subQ1=sQuery(id+"F0.wireOp",EDGE,"E3");var subQ2=makeQuery(id+"F0.imprint","INTERSECT",VERTEX,{"disambiguationData":[OD(1.0)],"derivedFrom":[subQ1,subQ0]});Q2=makeQuery(id+"F0.imprint","IMPRINT",FACE,{"disambiguationData":[TD([[makeQuery(id+"F0.imprint","IMPRINT",EDGE,{"disambiguationData":[TD([[subQ2,-1.0]])],"derivedFrom":subQ1}),1.0]])]});}
            var Q3;
            {var subQ5=sQuery(id+"F0.wireOp",EDGE,"E19");var subQ6=makeQuery(id+"F0.imprint","IMPRINT",VERTEX,{"derivedFrom":subQ5});Q3=makeQuery(id+"F0.imprint","IMPRINT",FACE,{"disambiguationData":[TD([[makeQuery(id+"F0.imprint","IMPRINT",EDGE,{"disambiguationData":[TD([[subQ6,1.0]])],"derivedFrom":subQ5}),-1.0]])]});}
            var Q4;
            {var subQ0=sQuery(id+"F0.wireOp",EDGE,"E9");var subQ1=sQuery(id+"F0.wireOp",EDGE,"E3");var subQ2=makeQuery(id+"F0.imprint","INTERSECT",VERTEX,{"derivedFrom":[subQ1,subQ0]});Q4=makeQuery(id+"F0.imprint","IMPRINT",FACE,{"disambiguationData":[TD([[makeQuery(id+"F0.imprint","IMPRINT",EDGE,{"disambiguationData":[TD([[subQ2,-1.0]])],"derivedFrom":subQ1}),1.0]])]});}
            extrude(context, id + "F4", {"entities" : qUnion([Q0, Q1, Q2, Q3, Q4]), "depth" : 19.43 * mm, "hasSecondDirection" : true, "secondDirectionOppositeDirection" : false, "secondDirectionDepth" : 12.7 * mm});
        }
        {
            var Q0;
            Q0=makeQuery(id+"F0.imprint","IMPRINT",FACE,{"disambiguationData":[TD([[makeQuery(id+"F0.imprint","IMPRINT",EDGE,{"derivedFrom":sQuery(id+"F0.wireOp",EDGE,"E6")}),1.0]])]});
            extrude(context, id + "F5", {"entities" : qUnion([Q0]), "oppositeDirection" : true, "depth" : 31.75 * mm, "hasSecondDirection" : true, "secondDirectionOppositeDirection" : true, "secondDirectionDepth" : 6.35 * mm});
        }
        {
            var Q0;
            {var subQ3=sQuery(id+"F0.wireOp",EDGE,"E15");Q0=makeQuery(id+"F0.imprint","IMPRINT",FACE,{"disambiguationData":[TD([[makeQuery(id+"F0.imprint","IMPRINT",EDGE,{"derivedFrom":subQ3}),-1.0]])]});}
            extrude(context, id + "F6", {"entities" : qUnion([Q0]), "depth" : 6.35 * mm});
        }
        {
            var Q0;
            Q0=makeQuery(id+"F6.opExtrude","CAP_FACE",FACE,{"disambiguationData":[OSD([sQuery(id+"F0.wireOp",EDGE,"E5.bottom"),sQuery(id+"F0.wireOp",EDGE,"E5.left"),sQuery(id+"F0.wireOp",EDGE,"E15")])],"isStart":false});
            extrude(context, id + "F7", {"entities" : qUnion([Q0]), "depth" : 3.17 * mm});
        }
        {
            var Q0;
            {var subQ0=sQuery(id+"F0.wireOp",EDGE,"E16");Q0=makeQuery(id+"F0.imprint","IMPRINT",FACE,{"disambiguationData":[TD([[makeQuery(id+"F0.imprint","IMPRINT",EDGE,{"derivedFrom":subQ0}),1.0]])]});}
            extrude(context, id + "F8", {"entities" : qUnion([Q0]), "depth" : 6.35 * mm});
        }
        {
            var Q0;
            Q0=makeQuery(id+"F8.opExtrude","CAP_FACE",FACE,{"disambiguationData":[OSD([sQuery(id+"F0.wireOp",EDGE,"E5.bottom"),sQuery(id+"F0.wireOp",EDGE,"E16"),sQuery(id+"F0.wireOp",EDGE,"E17"),sQuery(id+"F0.wireOp",EDGE,"E18")])],"isStart":false});
            extrude(context, id + "F9", {"entities" : qUnion([Q0]), "depth" : 3.17 * mm});
        }
    });
